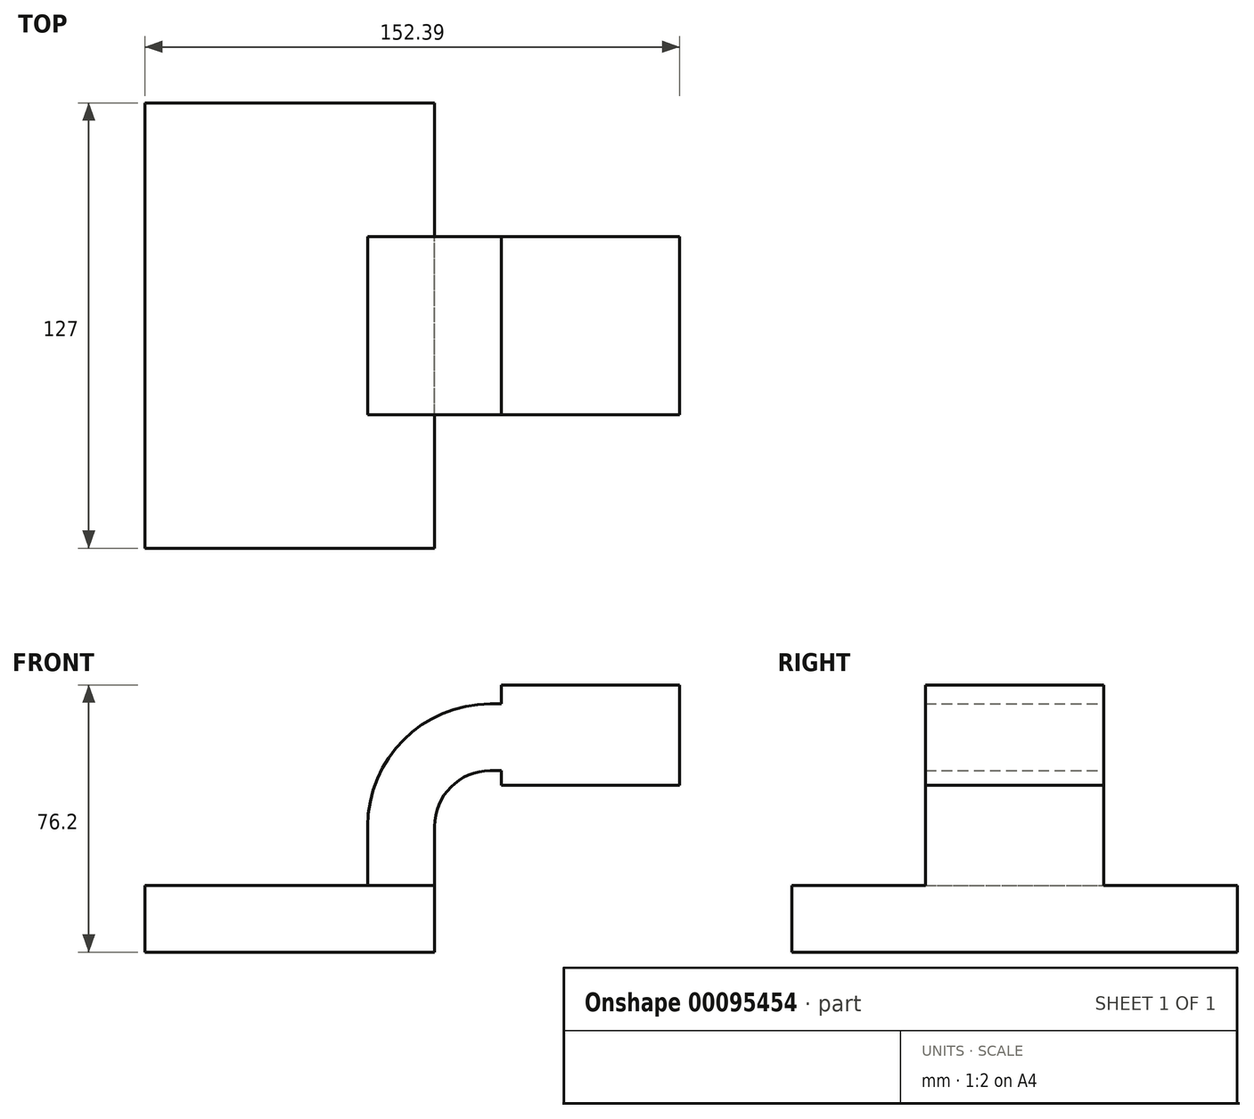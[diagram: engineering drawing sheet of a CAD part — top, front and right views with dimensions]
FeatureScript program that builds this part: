
annotation { "Feature Type Name" : "Feature", "Feature Type Description" : "" }
export const myFeature = defineFeature(function(context is Context, id is Id, definition is map)
    precondition{}
    {
        {
            var Q0;
            Q0=qCreatedBy(makeId("Front.planeOp"),FACE);
            var sketch = newSketch(context, id + "F0", { "sketchPlane" : qUnion([Q0])});
            skLineSegment(sketch, "E0.bottom", {"start": v(-41.28, 9.52) * mm, "end": v(41.27, 9.53) * mm});
            skLineSegment(sketch, "E0.top", {"start": v(-41.28, -9.53) * mm, "end": v(41.28, -9.53) * mm});
            skLineSegment(sketch, "E0.left", {"start": v(-41.28, 9.52) * mm, "end": v(-41.28, -9.53) * mm});
            skLineSegment(sketch, "E0.right", {"start": v(41.27, 9.53) * mm, "end": v(41.28, -9.52) * mm});
            skPoint(sketch, "E0.middle", {"position": v(0, 0) * mm});
            skLineSegment(sketch, "E1.bottom", {"start": v(60.32, 38.1) * mm, "end": v(111.12, 38.1) * mm});
            skLineSegment(sketch, "E1.top", {"start": v(60.32, 66.68) * mm, "end": v(111.12, 66.68) * mm});
            skLineSegment(sketch, "E1.left", {"start": v(60.32, 38.1) * mm, "end": v(60.32, 66.68) * mm});
            skLineSegment(sketch, "E1.right", {"start": v(111.12, 38.1) * mm, "end": v(111.12, 66.68) * mm});
            skPoint(sketch, "E1.middle", {"position": v(85.72, 52.39) * mm});
            skLineSegment(sketch, "E2", {"start": v(41.27, 9.53) * mm, "end": v(41.27, 26.31) * mm});
            skArc(sketch, "E3", {"start": v(41.27, 26.31) * mm, "mid": v(45.92, 37.54) * mm, "end": v(57.15, 42.19) * mm});
            skLineSegment(sketch, "E4", {"start": v(57.15, 42.19) * mm, "end": v(78.95, 42.19) * mm});
            skLineSegment(sketch, "E5.0", {"start": v(57.15, 61.24) * mm, "end": v(78.95, 61.24) * mm});
            skArc(sketch, "E5.1", {"start": v(22.22, 26.31) * mm, "mid": v(32.45, 51.01) * mm, "end": v(57.15, 61.24) * mm});
            skLineSegment(sketch, "E5.2", {"start": v(22.22, 9.53) * mm, "end": v(22.22, 26.31) * mm});
            skFitSpline(sketch, "E6", {"points": [v(-41.28, 9.52) * mm, v(57.15, 61.24) * mm], "startDerivative": vector(-2.23, 104.08) * mm, "endDerivative": vector(121.55, -0.2) * mm});
            skLineSegment(sketch, "E7", {"start": v(85.72, 52.39) * mm, "end": v(85.72, 66.68) * mm});
            skSolve(sketch);
        }
        {
            var Q0;
            Q0=makeQuery(id+"F0.imprint","IMPRINT",FACE,{"disambiguationData":[TD([[makeQuery(id+"F0.imprint","IMPRINT",EDGE,{"derivedFrom":sQuery(id+"F0.wireOp",EDGE,"E0.top")}),1.0]])]});
            extrude(context, id + "F1", {"entities" : qUnion([Q0]), "endBound" : BoundingType.SYMMETRIC, "depth" : 127 * mm});
        }
        {
            var Q0;
            {var subQ2=sQuery(id+"F0.wireOp",EDGE,"E2");Q0=makeQuery(id+"F0.imprint","IMPRINT",FACE,{"disambiguationData":[TD([[makeQuery(id+"F0.imprint","IMPRINT",EDGE,{"derivedFrom":subQ2}),1.0]])]});}
            var Q1;
            {var subQ3=sQuery(id+"F0.wireOp",EDGE,"E1.bottom");Q1=makeQuery(id+"F0.imprint","IMPRINT",FACE,{"disambiguationData":[TD([[makeQuery(id+"F0.imprint","IMPRINT",EDGE,{"derivedFrom":subQ3}),1.0]])]});}
            extrude(context, id + "F2", {"entities" : qUnion([Q0, Q1]), "operationType" : NewBodyOperationType.ADD, "endBound" : BoundingType.SYMMETRIC, "depth" : 50.8 * mm});
        }
    });
